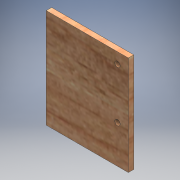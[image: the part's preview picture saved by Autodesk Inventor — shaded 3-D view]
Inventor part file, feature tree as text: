
AUTODESK INVENTOR PART (.ipt)
format: ipt  version: 2016 (Build 200138000, 138)  size: 124,928 bytes
history: native  units: mm
features: sketch x2, extrude x1, hole x1
ambient origin geometry x8: Origin, YZ Plane, XZ Plane, XY Plane, X Axis, Y Axis, Z Axis, Center Point
bodies: Solid1 (feature_tree)
feature tree (4):
  extrude  "Extrusion1"  Depth=55.0mm
  hole  "Hole1"  [1 undecoded]
  sketch  "Sketch1"  dims[d0=45.5mm d1=55.0mm]
  sketch  "Sketch2"  dims[d2=3.0mm d3=0.0mm d4=15.0mm d5=2.0mm d6=6.0mm d7=6.0mm d8=2.0mm d9=6.0mm d10=6.0mm d11=3.0mm d12=6.0mm d13=4.0mm d14=2.0mm d15=90.0deg d16=8.0mm d17=20.594885mm]
note: 1 required parameter value undecoded (feature->parameter linkage not recoverable at this tier; creation-order binding heuristic only, values carry confidence <= 0.55)
